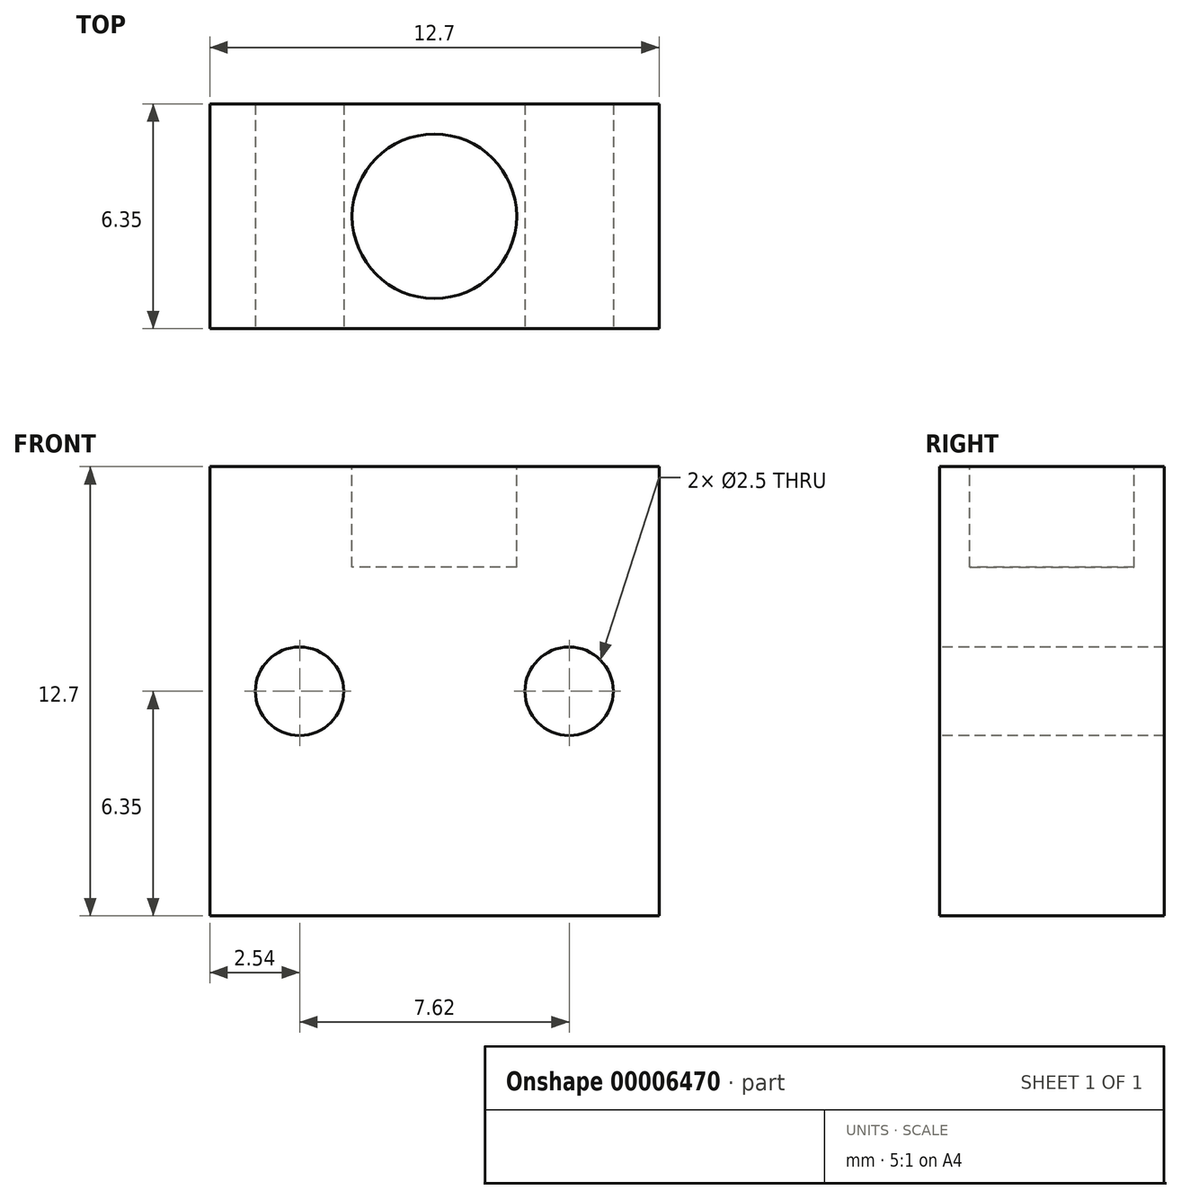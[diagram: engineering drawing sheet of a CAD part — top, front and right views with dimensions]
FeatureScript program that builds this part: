
annotation { "Feature Type Name" : "Feature", "Feature Type Description" : "" }
export const myFeature = defineFeature(function(context is Context, id is Id, definition is map)
    precondition{}
    {
        {
            var Q0;
            Q0=qCreatedBy(makeId("Front.planeOp"),FACE);
            var sketch = newSketch(context, id + "F0", { "sketchPlane" : qUnion([Q0])});
            skLineSegment(sketch, "E0.bottom", {"start": v(0, 0) * mm, "end": v(12.7, 0) * mm});
            skLineSegment(sketch, "E0.top", {"start": v(0, 12.7) * mm, "end": v(12.7, 12.7) * mm});
            skLineSegment(sketch, "E0.left", {"start": v(0, 0) * mm, "end": v(0, 12.7) * mm});
            skLineSegment(sketch, "E0.right", {"start": v(12.7, 0) * mm, "end": v(12.7, 12.7) * mm});
            skSolve(sketch);
        }
        {
            var Q0;
            Q0 = qSketchRegion(id + "F0", true);
            extrude(context, id + "F1", {"entities" : qUnion([Q0]), "depth" : 6.35 * mm});
        }
        {
            var Q0;
            Q0=makeQuery(id+"F1.opExtrude","CAP_FACE",FACE,{"disambiguationData":[OSD([sQuery(id+"F0.wireOp",EDGE,"E0.bottom"),sQuery(id+"F0.wireOp",EDGE,"E0.top"),sQuery(id+"F0.wireOp",EDGE,"E0.left"),sQuery(id+"F0.wireOp",EDGE,"E0.right")])],"isStart":false});
            var sketch = newSketch(context, id + "F2", { "sketchPlane" : qUnion([Q0])});
            skLineSegment(sketch, "E1", {"start": v(0, 6.35) * mm, "end": v(12.7, 6.35) * mm, "construction": true});
            skCircle(sketch, "E2", {"center": v(2.54, 6.35) * mm, "radius": 1.25 * mm});
            skCircle(sketch, "E3", {"center": v(10.16, 6.35) * mm, "radius": 1.25 * mm});
            skLineSegment(sketch, "E4", {"start": v(2.54, 6.35) * mm, "end": v(0, 12.7) * mm, "construction": true});
            skLineSegment(sketch, "E5", {"start": v(10.16, 6.35) * mm, "end": v(12.7, 12.7) * mm, "construction": true});
            skSolve(sketch);
        }
        {
            var Q0;
            Q0 = qSketchRegion(id + "F2", true);
            extrude(context, id + "F3", {"entities" : qUnion([Q0]), "operationType" : NewBodyOperationType.REMOVE, "endBound" : BoundingType.THROUGH_ALL, "oppositeDirection" : true, "depth" : 25.4 * mm});
        }
        {
            var Q0;
            Q0=makeQuery(id+"F1.opExtrude","SWEPT_FACE",FACE,{"disambiguationData":[OSD([sQuery(id+"F0.wireOp",EDGE,"E0.top")])]});
            var sketch = newSketch(context, id + "F4", { "sketchPlane" : qUnion([Q0])});
            skCircle(sketch, "E6", {"center": v(6.35, -3.18) * mm, "radius": 2.32 * mm});
            skLineSegment(sketch, "E7", {"start": v(0, -3.18) * mm, "end": v(6.35, -3.18) * mm, "construction": true});
            skLineSegment(sketch, "E8", {"start": v(12.7, -3.18) * mm, "end": v(6.35, -3.18) * mm, "construction": true});
            skSolve(sketch);
        }
        {
            var Q0;
            Q0 = qSketchRegion(id + "F4", true);
            extrude(context, id + "F5", {"entities" : qUnion([Q0]), "operationType" : NewBodyOperationType.REMOVE, "oppositeDirection" : true, "depth" : 2.84 * mm});
        }
    });
